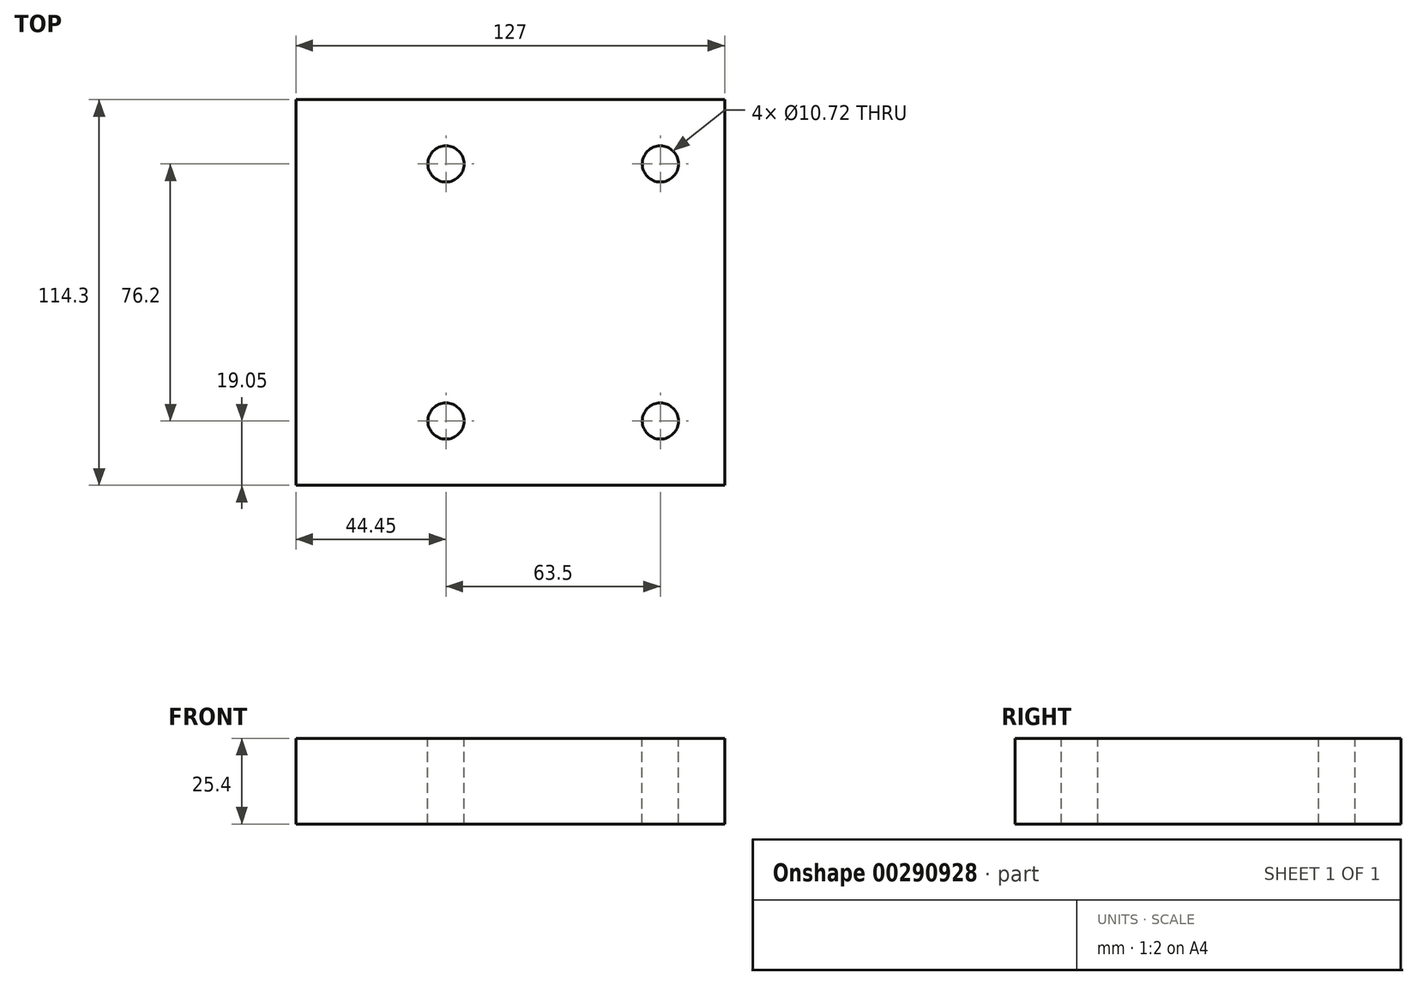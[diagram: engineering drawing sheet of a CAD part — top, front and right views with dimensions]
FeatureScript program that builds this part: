
annotation { "Feature Type Name" : "Feature", "Feature Type Description" : "" }
export const myFeature = defineFeature(function(context is Context, id is Id, definition is map)
    precondition{}
    {
        {
            var Q0;
            Q0=qCreatedBy(makeId("Top.planeOp"),FACE);
            var sketch = newSketch(context, id + "F0", { "sketchPlane" : qUnion([Q0])});
            skLineSegment(sketch, "E0.bottom", {"start": v(-63.5, 57.15) * mm, "end": v(63.5, 57.15) * mm});
            skLineSegment(sketch, "E0.top", {"start": v(-63.5, -57.15) * mm, "end": v(63.5, -57.15) * mm});
            skLineSegment(sketch, "E0.left", {"start": v(-63.5, 57.15) * mm, "end": v(-63.5, -57.15) * mm});
            skLineSegment(sketch, "E0.right", {"start": v(63.5, 57.15) * mm, "end": v(63.5, -57.15) * mm});
            skPoint(sketch, "E0.middle", {"position": v(0, 0) * mm});
            skSolve(sketch);
        }
        {
            var Q0;
            Q0 = qSketchRegion(id + "F0", true);
            extrude(context, id + "F1", {"entities" : qUnion([Q0]), "depth" : 25.4 * mm});
        }
        {
            var Q0;
            Q0=makeQuery(id+"F1.opExtrude","CAP_FACE",FACE,{"disambiguationData":[OSD([sQuery(id+"F0.wireOp",EDGE,"E0.bottom"),sQuery(id+"F0.wireOp",EDGE,"E0.top"),sQuery(id+"F0.wireOp",EDGE,"E0.left"),sQuery(id+"F0.wireOp",EDGE,"E0.right")])],"isStart":false});
            var sketch = newSketch(context, id + "F2", { "sketchPlane" : qUnion([Q0])});
            skLineSegment(sketch, "E1.0", {"start": v(63.5, 57.15) * mm, "end": v(63.5, -57.15) * mm, "construction": true});
            skLineSegment(sketch, "E2", {"start": v(-120.34, 0) * mm, "end": v(130.27, 0) * mm, "construction": true});
            skLineSegment(sketch, "E3.0", {"start": v(44.45, 57.15) * mm, "end": v(44.45, -57.15) * mm, "construction": true});
            skLineSegment(sketch, "E4.0", {"start": v(-19.05, 57.15) * mm, "end": v(-19.05, -57.15) * mm, "construction": true});
            skLineSegment(sketch, "E5.0", {"start": v(-120.34, -38.1) * mm, "end": v(130.27, -38.1) * mm, "construction": true});
            skPoint(sketch, "E6", {"position": v(-19.05, -38.1) * mm});
            skPoint(sketch, "E7", {"position": v(44.45, -38.1) * mm});
            skPoint(sketch, "E8.MirrorP", {"position": v(-19.05, 38.1) * mm});
            skPoint(sketch, "E9.MirrorP", {"position": v(44.45, 38.1) * mm});
            skSolve(sketch);
        }
        {
            var Q0;
            Q0=sQuery(id+"F2.wireOp",VERTEX,"E8.MirrorP");
            var Q1;
            Q1=sQuery(id+"F2.wireOp",VERTEX,"E9.MirrorP");
            var Q2;
            Q2=sQuery(id+"F2.wireOp",VERTEX,"E6");
            var Q3;
            Q3=sQuery(id+"F2.wireOp",VERTEX,"E7");
            var Q4;
            Q4=makeQuery(id+"F1.opExtrude","SWEPT_BODY",BODY,{"disambiguationData":[OSD([sQuery(id+"F0.wireOp",EDGE,"E0.bottom"),sQuery(id+"F0.wireOp",EDGE,"E0.top"),sQuery(id+"F0.wireOp",EDGE,"E0.left"),sQuery(id+"F0.wireOp",EDGE,"E0.right")])]});
            hole(context, id + "F3", {"style" : HoleStyle.SIMPLE, "endStyle" : HoleEndStyle.THROUGH, "standardTappedOrClearance" : lookupTablePath({ "standard" : "ANSI", "engagement" : "75%", "pitch" : "13 tpi", "size" : "1/2", "type" : "Tapped" }), "standardBlindInLast" : lookupTablePath({ "standard" : "ANSI", "engagement" : "75%", "pitch" : "13 tpi", "size" : "1/2", "type" : "Tapped" }), "holeDiameter" : 10.72 * mm, "showTappedDepth" : true, "tappedDepth" : 10 * mm, "tapClearance" : 3, "locations" : qUnion([Q0, Q1, Q2, Q3]), "scope" : qUnion([Q4]), "majorDiameter" : 12.7 * mm});
        }
    });
